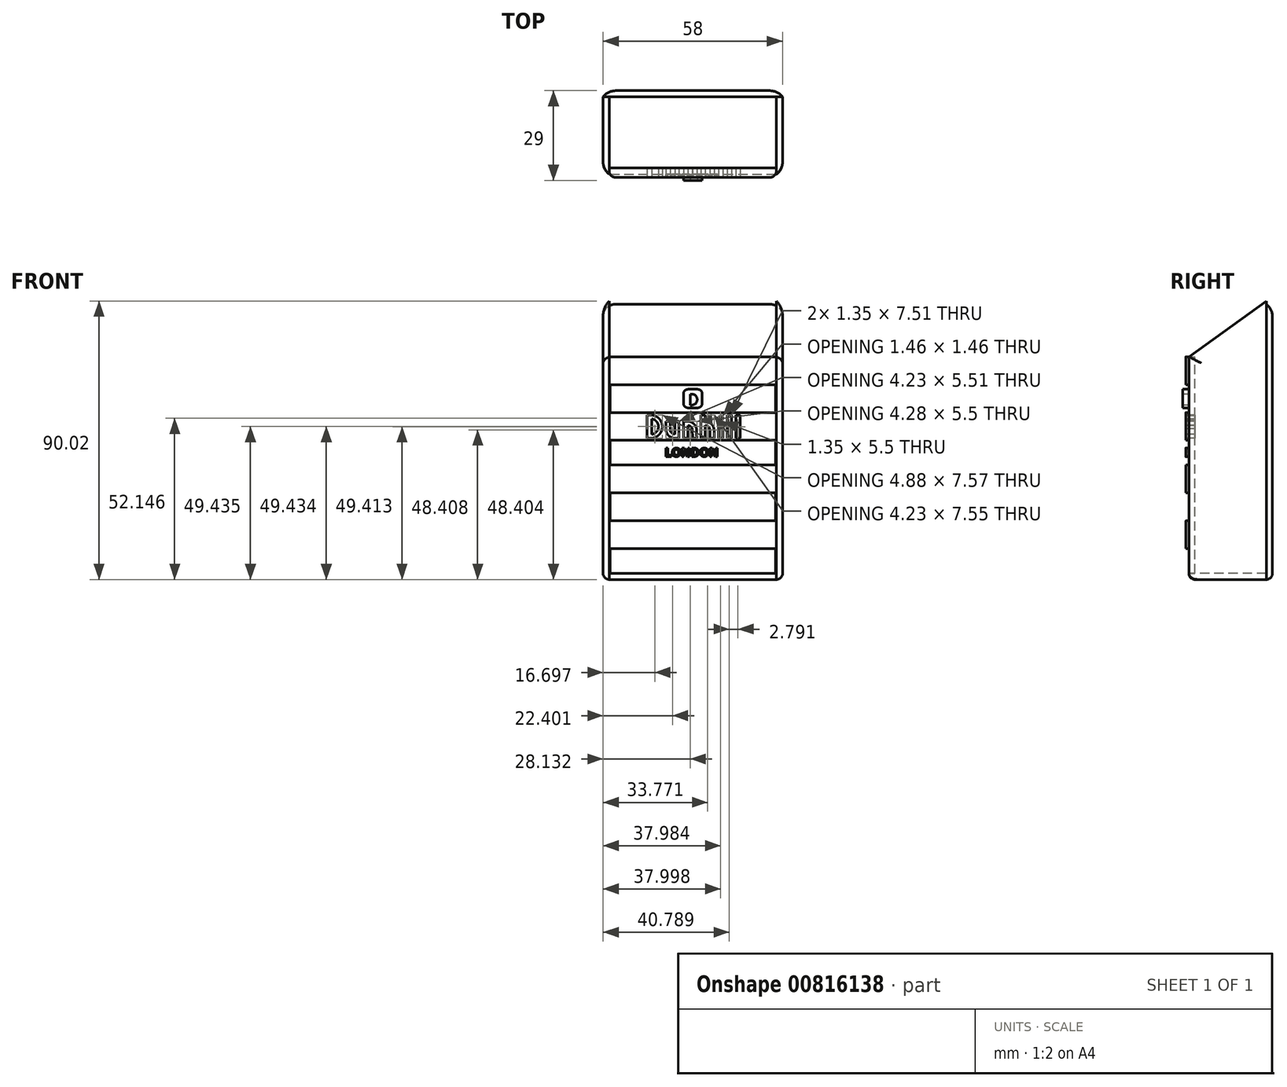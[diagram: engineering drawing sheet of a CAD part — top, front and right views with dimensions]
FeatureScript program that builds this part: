
annotation { "Feature Type Name" : "Feature", "Feature Type Description" : "" }
export const myFeature = defineFeature(function(context is Context, id is Id, definition is map)
    precondition{}
    {
        {
            var Q0;
            Q0=qCreatedBy(makeId("Top.planeOp"),FACE);
            var sketch = newSketch(context, id + "F0", { "sketchPlane" : qUnion([Q0])});
            skLineSegment(sketch, "E0.bottom", {"start": v(-3.76, 0) * mm, "end": v(50.24, 0) * mm});
            skLineSegment(sketch, "E0.top", {"start": v(-3.76, -25) * mm, "end": v(50.24, -25) * mm});
            skLineSegment(sketch, "E0.left", {"start": v(-3.76, 0) * mm, "end": v(-3.76, -25) * mm});
            skLineSegment(sketch, "E0.right", {"start": v(50.24, 0) * mm, "end": v(50.24, -25) * mm});
            skSolve(sketch);
        }
        {
            var Q0;
            Q0=qCreatedBy(makeId("Front.planeOp"),FACE);
            var sketch = newSketch(context, id + "F1", { "sketchPlane" : qUnion([Q0])});
            skLineSegment(sketch, "E1.bottom", {"start": v(-5.76, -2) * mm, "end": v(52.24, -2) * mm});
            skLineSegment(sketch, "E1.top", {"start": v(-5.76, 88) * mm, "end": v(52.24, 88) * mm});
            skLineSegment(sketch, "E1.left", {"start": v(-5.76, -2) * mm, "end": v(-5.76, 88) * mm});
            skLineSegment(sketch, "E1.right", {"start": v(52.24, -2) * mm, "end": v(52.24, 88) * mm});
            skSolve(sketch);
        }
        {
            var Q0;
            Q0=makeQuery(id+"F0.imprint","IMPRINT",FACE,{"disambiguationData":[TD([[makeQuery(id+"F0.imprint","IMPRINT",EDGE,{"derivedFrom":sQuery(id+"F0.wireOp",EDGE,"E0.bottom")}),-1.0]])]});
            extrude(context, id + "F2", {"entities" : qUnion([Q0]), "oppositeDirection" : true, "depth" : 2 * mm, "offsetDistance" : 25 * mm});
        }
        {
            var Q0;
            Q0=makeQuery(id+"F2.opExtrude","SWEPT_FACE",FACE,{"disambiguationData":[OSD([sQuery(id+"F0.wireOp",EDGE,"E0.top")])]});
            cPlane(context, id + "F3", {"entities" : qUnion([Q0]), "cplaneType" : CPlaneType.OFFSET, "offset" : 2 * mm, "oppositeDirection" : true, "width" : 150 * mm, "height" : 150 * mm});
        }
        {
            var Q0;
            Q0=qCreatedBy(id+"F3.planeOp",FACE);
            var sketch = newSketch(context, id + "F4", { "sketchPlane" : qUnion([Q0])});
            skLineSegment(sketch, "E2.bottom", {"start": v(-3.77, 0) * mm, "end": v(50.23, 0) * mm});
            skLineSegment(sketch, "E2.top", {"start": v(-3.77, 70) * mm, "end": v(50.23, 70) * mm});
            skLineSegment(sketch, "E2.left", {"start": v(-3.77, 0) * mm, "end": v(-3.77, 70) * mm});
            skLineSegment(sketch, "E2.right", {"start": v(50.23, 0) * mm, "end": v(50.23, 70) * mm});
            skSolve(sketch);
        }
        {
            var Q0;
            Q0=makeQuery(id+"F2.opExtrude","SWEPT_FACE",FACE,{"disambiguationData":[OSD([sQuery(id+"F0.wireOp",EDGE,"E0.right")])]});
            cPlane(context, id + "F5", {"entities" : qUnion([Q0]), "cplaneType" : CPlaneType.OFFSET, "offset" : 0 * mm, "width" : 150 * mm, "height" : 150 * mm});
        }
        {
            var Q0;
            Q0=qCreatedBy(id+"F5.planeOp",FACE);
            var sketch = newSketch(context, id + "F6", { "sketchPlane" : qUnion([Q0])});
            skLineSegment(sketch, "E3", {"start": v(-25, -2) * mm, "end": v(0, -2) * mm});
            skLineSegment(sketch, "E4", {"start": v(0, -2) * mm, "end": v(0, 88.02) * mm});
            skLineSegment(sketch, "E5", {"start": v(0, 88.02) * mm, "end": v(-25, 70) * mm});
            skLineSegment(sketch, "E6", {"start": v(-25, 70) * mm, "end": v(-25, -2) * mm});
            skSolve(sketch);
        }
        {
            var Q0;
            Q0=makeQuery(id+"F2.opExtrude","SWEPT_FACE",FACE,{"disambiguationData":[OSD([sQuery(id+"F0.wireOp",EDGE,"E0.left")])]});
            cPlane(context, id + "F7", {"entities" : qUnion([Q0]), "cplaneType" : CPlaneType.OFFSET, "offset" : 0 * mm, "width" : 150 * mm, "height" : 150 * mm});
        }
        {
            var Q0;
            Q0=qCreatedBy(id+"F7.planeOp",FACE);
            var sketch = newSketch(context, id + "F8", { "sketchPlane" : qUnion([Q0])});
            skLineSegment(sketch, "E7", {"start": v(0, -2) * mm, "end": v(24.96, -2) * mm});
            skLineSegment(sketch, "E8", {"start": v(24.96, -2) * mm, "end": v(24.96, 70) * mm});
            skLineSegment(sketch, "E9", {"start": v(24.96, 70) * mm, "end": v(0, 88) * mm});
            skLineSegment(sketch, "E10", {"start": v(0, 88) * mm, "end": v(0, -2) * mm});
            skSolve(sketch);
        }
        {
            var Q0;
            Q0=makeQuery(id+"F6.imprint","IMPRINT",FACE,{"disambiguationData":[TD([[makeQuery(id+"F6.imprint","IMPRINT",EDGE,{"derivedFrom":sQuery(id+"F6.wireOp",EDGE,"E3")}),1.0]])]});
            extrude(context, id + "F9", {"entities" : qUnion([Q0]), "depth" : 2 * mm, "offsetDistance" : 25 * mm});
        }
        {
            var Q0;
            Q0=makeQuery(id+"F4.imprint","IMPRINT",FACE,{"disambiguationData":[TD([[makeQuery(id+"F4.imprint","IMPRINT",EDGE,{"derivedFrom":sQuery(id+"F4.wireOp",EDGE,"E2.bottom")}),1.0]])]});
            extrude(context, id + "F10", {"entities" : qUnion([Q0]), "depth" : 2 * mm, "offsetDistance" : 25 * mm});
        }
        {
            var Q0;
            Q0=makeQuery(id+"F8.imprint","IMPRINT",FACE,{"disambiguationData":[TD([[makeQuery(id+"F8.imprint","IMPRINT",EDGE,{"derivedFrom":sQuery(id+"F8.wireOp",EDGE,"E7")}),1.0]])]});
            extrude(context, id + "F11", {"entities" : qUnion([Q0]), "depth" : 2 * mm, "offsetDistance" : 25 * mm});
        }
        {
            var Q0;
            Q0=makeQuery(id+"F1.imprint","IMPRINT",FACE,{"disambiguationData":[TD([[makeQuery(id+"F1.imprint","IMPRINT",EDGE,{"derivedFrom":sQuery(id+"F1.wireOp",EDGE,"E1.bottom")}),1.0]])]});
            extrude(context, id + "F12", {"entities" : qUnion([Q0]), "oppositeDirection" : true, "depth" : 2 * mm, "offsetDistance" : 25 * mm});
        }
        {
            var Q0;
            Q0=makeQuery(id+"F9.opExtrude","CAP_EDGE",EDGE,{"disambiguationData":[OSD([sQuery(id+"F6.wireOp",EDGE,"E6")])],"isStart":false});
            var Q1;
            Q1=makeQuery(id+"F11.opExtrude","CAP_EDGE",EDGE,{"disambiguationData":[OSD([sQuery(id+"F8.wireOp",EDGE,"E8")])],"isStart":false});
            var Q2;
            Q2=makeQuery(id+"F12.opExtrude","CAP_EDGE",EDGE,{"disambiguationData":[OSD([sQuery(id+"F1.wireOp",EDGE,"E1.left")])],"isStart":false});
            var Q3;
            Q3=makeQuery(id+"F12.opExtrude","CAP_EDGE",EDGE,{"disambiguationData":[OSD([sQuery(id+"F1.wireOp",EDGE,"E1.right")])],"isStart":false});
            fillet(context, id + "F13", {"entities" : qUnion([Q0, Q1, Q2, Q3]), "radius" : 5 * mm, "tangentPropagation" : true, "allowEdgeOverflow" : false});
        }
        {
            var Q0;
            Q0=makeQuery(id+"F12.opExtrude","CAP_EDGE",EDGE,{"disambiguationData":[OSD([sQuery(id+"F1.wireOp",EDGE,"E1.bottom")])],"isStart":false});
            var Q1;
            Q1=makeQuery(id+"F11.opExtrude","CAP_EDGE",EDGE,{"disambiguationData":[OSD([sQuery(id+"F8.wireOp",EDGE,"E7")])],"isStart":false});
            var Q2;
            Q2=makeQuery(id+"F9.opExtrude","CAP_EDGE",EDGE,{"disambiguationData":[OSD([sQuery(id+"F6.wireOp",EDGE,"E3")])],"isStart":false});
            fillet(context, id + "F14", {"entities" : qUnion([Q0, Q1, Q2]), "radius" : 2 * mm, "tangentPropagation" : true, "allowEdgeOverflow" : false});
        }
        {
            var Q0;
            Q0=makeQuery(id+"F2.opExtrude","CAP_EDGE",EDGE,{"disambiguationData":[OSD([sQuery(id+"F0.wireOp",EDGE,"E0.top")])],"isStart":false});
            fillet(context, id + "F15", {"entities" : qUnion([Q0]), "radius" : 2 * mm, "tangentPropagation" : true, "allowEdgeOverflow" : false});
        }
        {
            var Q0;
            {var subQ0=sQuery(id+"F4.wireOp",EDGE,"E2.bottom");var subQ1=sQuery(id+"F4.wireOp",EDGE,"E2.top");var subQ2=sQuery(id+"F4.wireOp",EDGE,"E2.left");var subQ3=sQuery(id+"F4.wireOp",EDGE,"E2.right");Q0=makeQuery(id+"F8PJ3iT0SF2CxUe_6.boolean.opBoolean","SPLIT",FACE,{"disambiguationData":[TD([makeQuery(id+"F10.opExtrude","SWEPT_FACE",FACE,{"disambiguationData":[OSD([subQ0])]})])],"derivedFrom":makeQuery(id+"F10.opExtrude","CAP_FACE",FACE,{"disambiguationData":[OSD([subQ0,subQ1,subQ2,subQ3])],"isStart":false})});}
            var sketch = newSketch(context, id + "F16", { "sketchPlane" : qUnion([Q0])});
            skLineSegment(sketch, "E11.bottom", {"start": v(-3.77, 70) * mm, "end": v(50.23, 70) * mm});
            skLineSegment(sketch, "E11.top", {"start": v(-3.77, 61) * mm, "end": v(50.23, 61) * mm});
            skLineSegment(sketch, "E11.left", {"start": v(-3.77, 70) * mm, "end": v(-3.77, 61) * mm});
            skLineSegment(sketch, "E11.right", {"start": v(50.23, 70) * mm, "end": v(50.23, 61) * mm});
            skLineSegment(sketch, "E12.top", {"start": v(-3.77, 52) * mm, "end": v(50.23, 52) * mm});
            skLineSegment(sketch, "E13.top", {"start": v(-3.77, 43) * mm, "end": v(50.23, 43) * mm});
            skLineSegment(sketch, "E13.left", {"start": v(-3.77, 52) * mm, "end": v(-3.77, 43) * mm});
            skLineSegment(sketch, "E13.right", {"start": v(50.23, 52) * mm, "end": v(50.23, 43) * mm});
            skLineSegment(sketch, "E14.bottom", {"start": v(50.23, 35) * mm, "end": v(-3.77, 35) * mm});
            skLineSegment(sketch, "E14.left", {"start": v(50.23, 35) * mm, "end": v(50.23, 26) * mm});
            skLineSegment(sketch, "E14.right", {"start": v(-3.77, 35) * mm, "end": v(-3.77, 26) * mm});
            skLineSegment(sketch, "E15.bottom", {"start": v(-3.77, 26) * mm, "end": v(50.23, 26) * mm});
            skLineSegment(sketch, "E15.top", {"start": v(-3.77, 17) * mm, "end": v(50.23, 17) * mm});
            skLineSegment(sketch, "E16.top", {"start": v(-3.77, 8) * mm, "end": v(50.23, 8) * mm});
            skLineSegment(sketch, "E16.left", {"start": v(-3.77, 17) * mm, "end": v(-3.77, 8) * mm});
            skLineSegment(sketch, "E16.right", {"start": v(50.23, 17) * mm, "end": v(50.23, 8) * mm});
            skSolve(sketch);
        }
        {
            var Q0;
            Q0=makeQuery(id+"F16.imprint","IMPRINT",FACE,{"disambiguationData":[TD([[makeQuery(id+"F16.imprint","IMPRINT",EDGE,{"derivedFrom":sQuery(id+"F16.wireOp",EDGE,"E11.bottom")}),-1.0]])]});
            var Q1;
            Q1=makeQuery(id+"F16.imprint","IMPRINT",FACE,{"disambiguationData":[TD([[makeQuery(id+"F16.imprint","IMPRINT",EDGE,{"derivedFrom":sQuery(id+"F16.wireOp",EDGE,"E12.top")}),-1.0]])]});
            var Q2;
            Q2=makeQuery(id+"F16.imprint","IMPRINT",FACE,{"disambiguationData":[TD([[makeQuery(id+"F16.imprint","IMPRINT",EDGE,{"derivedFrom":sQuery(id+"F16.wireOp",EDGE,"E14.bottom")}),1.0]])]});
            var Q3;
            Q3=makeQuery(id+"F16.imprint","IMPRINT",FACE,{"disambiguationData":[TD([[makeQuery(id+"F16.imprint","IMPRINT",EDGE,{"derivedFrom":sQuery(id+"F16.wireOp",EDGE,"E15.top")}),-1.0]])]});
            extrude(context, id + "F17", {"entities" : qUnion([Q0, Q1, Q2, Q3]), "operationType" : NewBodyOperationType.ADD, "depth" : 1 * mm, "offsetDistance" : 25 * mm});
        }
        {
            var Q0;
            Q0=makeQuery(id+"F17.opExtrude","CAP_EDGE",EDGE,{"disambiguationData":[OSD([sQuery(id+"F16.wireOp",EDGE,"E11.left")])],"isStart":false});
            var Q1;
            Q1=makeQuery(id+"F17.opExtrude","CAP_EDGE",EDGE,{"disambiguationData":[OSD([sQuery(id+"F16.wireOp",EDGE,"E13.left")])],"isStart":false});
            var Q2;
            Q2=makeQuery(id+"F17.opExtrude","CAP_EDGE",EDGE,{"disambiguationData":[OSD([sQuery(id+"F16.wireOp",EDGE,"E14.right")])],"isStart":false});
            var Q3;
            Q3=makeQuery(id+"F17.opExtrude","CAP_EDGE",EDGE,{"disambiguationData":[OSD([sQuery(id+"F16.wireOp",EDGE,"E16.left")])],"isStart":false});
            var Q4;
            Q4=makeQuery(id+"F17.opExtrude","CAP_EDGE",EDGE,{"disambiguationData":[OSD([sQuery(id+"F16.wireOp",EDGE,"E16.right")])],"isStart":false});
            var Q5;
            Q5=makeQuery(id+"F17.opExtrude","CAP_EDGE",EDGE,{"disambiguationData":[OSD([sQuery(id+"F16.wireOp",EDGE,"E14.left")])],"isStart":false});
            var Q6;
            Q6=makeQuery(id+"F17.opExtrude","CAP_EDGE",EDGE,{"disambiguationData":[OSD([sQuery(id+"F16.wireOp",EDGE,"E13.right")])],"isStart":false});
            var Q7;
            Q7=makeQuery(id+"F17.opExtrude","CAP_EDGE",EDGE,{"disambiguationData":[OSD([sQuery(id+"F16.wireOp",EDGE,"E11.right")])],"isStart":false});
            fillet(context, id + "F18", {"entities" : qUnion([Q0, Q1, Q2, Q3, Q4, Q5, Q6, Q7]), "radius" : 2 * mm, "tangentPropagation" : true, "allowEdgeOverflow" : false});
        }
        {
            var Q0;
            Q0=makeQuery(id+"F17.opExtrude","CAP_FACE",FACE,{"disambiguationData":[OSD([sQuery(id+"F16.wireOp",EDGE,"E12.top"),sQuery(id+"F16.wireOp",EDGE,"E13.top"),sQuery(id+"F16.wireOp",EDGE,"E13.left"),sQuery(id+"F16.wireOp",EDGE,"E13.right")])],"isStart":false});
            var sketch = newSketch(context, id + "F19", { "sketchPlane" : qUnion([Q0])});
            skLineSegment(sketch, "E17", {"start": v(8.5, 47.43) * mm, "end": v(8.5, 43.65) * mm});
            skLineSegment(sketch, "E18", {"start": v(8.5, 43.65) * mm, "end": v(9.37, 43.67) * mm});
            skArc(sketch, "E19", {"start": v(9.37, 43.67) * mm, "mid": v(9.7, 43.68) * mm, "end": v(10.05, 43.7) * mm});
            skArc(sketch, "E20", {"start": v(10.05, 43.7) * mm, "mid": v(10.27, 43.72) * mm, "end": v(10.49, 43.76) * mm});
            skArc(sketch, "E21", {"start": v(10.49, 43.76) * mm, "mid": v(10.68, 43.8) * mm, "end": v(10.86, 43.87) * mm});
            skArc(sketch, "E22", {"start": v(10.86, 43.87) * mm, "mid": v(11.09, 43.96) * mm, "end": v(11.3, 44.07) * mm});
            skArc(sketch, "E23", {"start": v(11.3, 44.07) * mm, "mid": v(11.65, 44.26) * mm, "end": v(11.96, 44.48) * mm});
            skArc(sketch, "E24", {"start": v(11.96, 44.48) * mm, "mid": v(12.25, 44.74) * mm, "end": v(12.51, 45.02) * mm});
            skArc(sketch, "E25", {"start": v(12.51, 45.02) * mm, "mid": v(12.74, 45.33) * mm, "end": v(12.94, 45.66) * mm});
            skArc(sketch, "E26", {"start": v(12.94, 45.66) * mm, "mid": v(13.1, 46.02) * mm, "end": v(13.24, 46.39) * mm});
            skArc(sketch, "E27", {"start": v(13.24, 46.39) * mm, "mid": v(13.3, 46.6) * mm, "end": v(13.33, 46.8) * mm});
            skArc(sketch, "E28", {"start": v(13.33, 46.8) * mm, "mid": v(13.36, 47.04) * mm, "end": v(13.37, 47.27) * mm});
            skArc(sketch, "E29", {"start": v(13.37, 47.27) * mm, "mid": v(13.38, 47.5) * mm, "end": v(13.37, 47.74) * mm});
            skArc(sketch, "E30", {"start": v(13.37, 47.74) * mm, "mid": v(13.34, 47.96) * mm, "end": v(13.3, 48.17) * mm});
            skArc(sketch, "E31", {"start": v(13.3, 48.17) * mm, "mid": v(13.2, 48.6) * mm, "end": v(13.03, 49.01) * mm});
            skArc(sketch, "E32", {"start": v(13.03, 49.01) * mm, "mid": v(12.82, 49.4) * mm, "end": v(12.57, 49.76) * mm});
            skArc(sketch, "E33", {"start": v(12.57, 49.76) * mm, "mid": v(12.28, 50.08) * mm, "end": v(11.95, 50.37) * mm});
            skArc(sketch, "E34", {"start": v(11.95, 50.37) * mm, "mid": v(11.59, 50.63) * mm, "end": v(11.2, 50.84) * mm});
            skArc(sketch, "E35", {"start": v(11.2, 50.84) * mm, "mid": v(11, 50.93) * mm, "end": v(10.79, 51) * mm});
            skArc(sketch, "E36", {"start": v(10.79, 51) * mm, "mid": v(10.6, 51.06) * mm, "end": v(10.4, 51.1) * mm});
            skArc(sketch, "E37", {"start": v(10.4, 51.1) * mm, "mid": v(10.19, 51.14) * mm, "end": v(9.96, 51.17) * mm});
            skArc(sketch, "E38", {"start": v(9.96, 51.17) * mm, "mid": v(9.65, 51.18) * mm, "end": v(9.33, 51.2) * mm});
            skLineSegment(sketch, "E39", {"start": v(9.33, 51.2) * mm, "end": v(8.5, 51.22) * mm});
            skLineSegment(sketch, "E40", {"start": v(8.5, 51.22) * mm, "end": v(8.5, 47.43) * mm});
            skArc(sketch, "E41", {"start": v(10.45, 49.8) * mm, "mid": v(10.71, 49.7) * mm, "end": v(10.96, 49.56) * mm});
            skArc(sketch, "E42", {"start": v(10.96, 49.56) * mm, "mid": v(11.2, 49.38) * mm, "end": v(11.42, 49.18) * mm});
            skArc(sketch, "E43", {"start": v(11.42, 49.18) * mm, "mid": v(11.62, 48.95) * mm, "end": v(11.8, 48.7) * mm});
            skArc(sketch, "E44", {"start": v(11.8, 48.7) * mm, "mid": v(11.93, 48.43) * mm, "end": v(12.04, 48.15) * mm});
            skArc(sketch, "E45", {"start": v(12.04, 48.15) * mm, "mid": v(12.08, 47.98) * mm, "end": v(12.11, 47.8) * mm});
            skArc(sketch, "E46", {"start": v(12.11, 47.8) * mm, "mid": v(12.13, 47.6) * mm, "end": v(12.13, 47.4) * mm});
            skArc(sketch, "E47", {"start": v(12.13, 47.4) * mm, "mid": v(12.12, 47.2) * mm, "end": v(12.1, 47) * mm});
            skArc(sketch, "E48", {"start": v(12.1, 47) * mm, "mid": v(12.06, 46.81) * mm, "end": v(12.01, 46.63) * mm});
            skArc(sketch, "E49", {"start": v(12.01, 46.63) * mm, "mid": v(11.9, 46.35) * mm, "end": v(11.74, 46.08) * mm});
            skArc(sketch, "E50", {"start": v(11.74, 46.08) * mm, "mid": v(11.56, 45.83) * mm, "end": v(11.35, 45.6) * mm});
            skArc(sketch, "E51", {"start": v(11.35, 45.6) * mm, "mid": v(11.12, 45.4) * mm, "end": v(10.87, 45.24) * mm});
            skArc(sketch, "E52", {"start": v(10.87, 45.24) * mm, "mid": v(10.6, 45.1) * mm, "end": v(10.3, 45) * mm});
            skArc(sketch, "E53", {"start": v(10.3, 45) * mm, "mid": v(10.19, 44.98) * mm, "end": v(10.07, 44.99) * mm});
            skArc(sketch, "E54", {"start": v(10.07, 44.99) * mm, "mid": v(10, 45.03) * mm, "end": v(9.96, 45.1) * mm});
            skArc(sketch, "E55", {"start": v(9.96, 45.1) * mm, "mid": v(9.94, 45.28) * mm, "end": v(9.94, 45.46) * mm});
            skArc(sketch, "E56", {"start": v(9.94, 45.46) * mm, "mid": v(9.93, 46.45) * mm, "end": v(9.93, 47.43) * mm});
            skLineSegment(sketch, "E57", {"start": v(9.93, 47.43) * mm, "end": v(9.93, 49.93) * mm});
            skLineSegment(sketch, "E58", {"start": v(9.93, 49.93) * mm, "end": v(10.07, 49.91) * mm});
            skArc(sketch, "E59", {"start": v(10.07, 49.91) * mm, "mid": v(10.1, 49.9) * mm, "end": v(10.13, 49.9) * mm});
            skArc(sketch, "E60", {"start": v(10.13, 49.9) * mm, "mid": v(10.18, 49.88) * mm, "end": v(10.23, 49.87) * mm});
            skArc(sketch, "E61", {"start": v(10.23, 49.87) * mm, "mid": v(10.29, 49.85) * mm, "end": v(10.34, 49.84) * mm});
            skArc(sketch, "E62", {"start": v(10.34, 49.84) * mm, "mid": v(10.4, 49.82) * mm, "end": v(10.45, 49.8) * mm});
            skLineSegment(sketch, "E63", {"start": v(25.9, 47.43) * mm, "end": v(25.9, 43.66) * mm});
            skLineSegment(sketch, "E64", {"start": v(25.9, 43.66) * mm, "end": v(26.57, 43.66) * mm});
            skLineSegment(sketch, "E65", {"start": v(26.57, 43.66) * mm, "end": v(27.25, 43.66) * mm});
            skLineSegment(sketch, "E66", {"start": v(27.25, 43.66) * mm, "end": v(27.25, 45.74) * mm});
            skLineSegment(sketch, "E67", {"start": v(27.25, 45.74) * mm, "end": v(27.25, 47.81) * mm});
            skLineSegment(sketch, "E68", {"start": v(27.25, 47.81) * mm, "end": v(27.46, 47.79) * mm});
            skArc(sketch, "E69", {"start": v(27.46, 47.79) * mm, "mid": v(27.62, 47.76) * mm, "end": v(27.78, 47.71) * mm});
            skArc(sketch, "E70", {"start": v(27.78, 47.71) * mm, "mid": v(27.94, 47.64) * mm, "end": v(28.09, 47.55) * mm});
            skArc(sketch, "E71", {"start": v(28.09, 47.55) * mm, "mid": v(28.22, 47.45) * mm, "end": v(28.35, 47.33) * mm});
            skArc(sketch, "E72", {"start": v(28.35, 47.33) * mm, "mid": v(28.45, 47.21) * mm, "end": v(28.54, 47.07) * mm});
            skArc(sketch, "E73", {"start": v(28.54, 47.07) * mm, "mid": v(28.6, 46.93) * mm, "end": v(28.67, 46.77) * mm});
            skArc(sketch, "E74", {"start": v(28.67, 46.77) * mm, "mid": v(28.7, 46.62) * mm, "end": v(28.73, 46.46) * mm});
            skArc(sketch, "E75", {"start": v(28.73, 46.46) * mm, "mid": v(28.75, 46.22) * mm, "end": v(28.76, 46) * mm});
            skArc(sketch, "E76", {"start": v(28.76, 46) * mm, "mid": v(28.77, 45.5) * mm, "end": v(28.77, 45.02) * mm});
            skLineSegment(sketch, "E77", {"start": v(28.77, 45.02) * mm, "end": v(28.77, 43.66) * mm});
            skLineSegment(sketch, "E78", {"start": v(28.77, 43.66) * mm, "end": v(29.45, 43.66) * mm});
            skLineSegment(sketch, "E79", {"start": v(29.45, 43.66) * mm, "end": v(30.12, 43.66) * mm});
            skLineSegment(sketch, "E80", {"start": v(30.12, 43.66) * mm, "end": v(30.12, 45.02) * mm});
            skArc(sketch, "E81", {"start": v(30.12, 45.02) * mm, "mid": v(30.12, 45.3) * mm, "end": v(30.12, 45.57) * mm});
            skArc(sketch, "E82", {"start": v(30.12, 45.57) * mm, "mid": v(30.12, 45.82) * mm, "end": v(30.11, 46.07) * mm});
            skArc(sketch, "E83", {"start": v(30.11, 46.07) * mm, "mid": v(30.1, 46.27) * mm, "end": v(30.1, 46.48) * mm});
            skArc(sketch, "E84", {"start": v(30.1, 46.48) * mm, "mid": v(30.1, 46.57) * mm, "end": v(30.08, 46.65) * mm});
            skArc(sketch, "E85", {"start": v(30.08, 46.65) * mm, "mid": v(30, 47.02) * mm, "end": v(29.87, 47.37) * mm});
            skArc(sketch, "E86", {"start": v(29.87, 47.37) * mm, "mid": v(29.7, 47.7) * mm, "end": v(29.5, 48) * mm});
            skArc(sketch, "E87", {"start": v(29.5, 48) * mm, "mid": v(29.26, 48.28) * mm, "end": v(28.98, 48.53) * mm});
            skArc(sketch, "E88", {"start": v(28.98, 48.53) * mm, "mid": v(28.67, 48.74) * mm, "end": v(28.33, 48.92) * mm});
            skArc(sketch, "E89", {"start": v(28.33, 48.92) * mm, "mid": v(28.22, 48.97) * mm, "end": v(28.1, 49) * mm});
            skArc(sketch, "E90", {"start": v(28.1, 49) * mm, "mid": v(27.97, 49.05) * mm, "end": v(27.84, 49.09) * mm});
            skArc(sketch, "E91", {"start": v(27.84, 49.09) * mm, "mid": v(27.72, 49.12) * mm, "end": v(27.6, 49.14) * mm});
            skArc(sketch, "E92", {"start": v(27.6, 49.14) * mm, "mid": v(27.5, 49.15) * mm, "end": v(27.4, 49.16) * mm});
            skLineSegment(sketch, "E93", {"start": v(27.4, 49.16) * mm, "end": v(27.25, 49.16) * mm});
            skLineSegment(sketch, "E94", {"start": v(27.25, 49.16) * mm, "end": v(27.25, 50.18) * mm});
            skLineSegment(sketch, "E95", {"start": v(27.25, 50.18) * mm, "end": v(27.25, 51.2) * mm});
            skLineSegment(sketch, "E96", {"start": v(27.25, 51.2) * mm, "end": v(26.57, 51.2) * mm});
            skLineSegment(sketch, "E97", {"start": v(26.57, 51.2) * mm, "end": v(25.9, 51.2) * mm});
            skLineSegment(sketch, "E98", {"start": v(25.9, 51.2) * mm, "end": v(25.9, 47.43) * mm});
            skLineSegment(sketch, "E99", {"start": v(34.35, 47.41) * mm, "end": v(34.35, 43.66) * mm});
            skLineSegment(sketch, "E100", {"start": v(34.35, 43.66) * mm, "end": v(35.03, 43.66) * mm});
            skLineSegment(sketch, "E101", {"start": v(35.03, 43.66) * mm, "end": v(35.7, 43.66) * mm});
            skLineSegment(sketch, "E102", {"start": v(35.7, 43.66) * mm, "end": v(35.7, 47.41) * mm});
            skLineSegment(sketch, "E103", {"start": v(35.7, 47.41) * mm, "end": v(35.7, 51.17) * mm});
            skLineSegment(sketch, "E104", {"start": v(35.7, 51.17) * mm, "end": v(35.03, 51.17) * mm});
            skLineSegment(sketch, "E105", {"start": v(35.03, 51.17) * mm, "end": v(34.35, 51.17) * mm});
            skLineSegment(sketch, "E106", {"start": v(34.35, 51.17) * mm, "end": v(34.35, 47.41) * mm});
            skLineSegment(sketch, "E107", {"start": v(37.14, 47.41) * mm, "end": v(37.14, 43.66) * mm});
            skLineSegment(sketch, "E108", {"start": v(37.14, 43.66) * mm, "end": v(37.82, 43.66) * mm});
            skLineSegment(sketch, "E109", {"start": v(37.82, 43.66) * mm, "end": v(38.5, 43.66) * mm});
            skLineSegment(sketch, "E110", {"start": v(38.5, 43.66) * mm, "end": v(38.5, 47.41) * mm});
            skLineSegment(sketch, "E111", {"start": v(38.5, 47.41) * mm, "end": v(38.5, 51.17) * mm});
            skLineSegment(sketch, "E112", {"start": v(38.5, 51.17) * mm, "end": v(37.82, 51.17) * mm});
            skLineSegment(sketch, "E113", {"start": v(37.82, 51.17) * mm, "end": v(37.14, 51.17) * mm});
            skLineSegment(sketch, "E114", {"start": v(37.14, 51.17) * mm, "end": v(37.14, 47.41) * mm});
            skArc(sketch, "E115", {"start": v(31.9, 50.8) * mm, "mid": v(31.75, 50.7) * mm, "end": v(31.63, 50.57) * mm});
            skArc(sketch, "E116", {"start": v(31.63, 50.57) * mm, "mid": v(31.55, 50.43) * mm, "end": v(31.5, 50.26) * mm});
            skArc(sketch, "E117", {"start": v(31.5, 50.26) * mm, "mid": v(31.5, 50.1) * mm, "end": v(31.53, 49.92) * mm});
            skArc(sketch, "E118", {"start": v(31.53, 49.92) * mm, "mid": v(31.6, 49.77) * mm, "end": v(31.72, 49.63) * mm});
            skArc(sketch, "E119", {"start": v(31.72, 49.63) * mm, "mid": v(31.85, 49.52) * mm, "end": v(32, 49.45) * mm});
            skArc(sketch, "E120", {"start": v(32, 49.45) * mm, "mid": v(32.17, 49.42) * mm, "end": v(32.34, 49.42) * mm});
            skArc(sketch, "E121", {"start": v(32.34, 49.42) * mm, "mid": v(32.5, 49.47) * mm, "end": v(32.65, 49.55) * mm});
            skArc(sketch, "E122", {"start": v(32.65, 49.55) * mm, "mid": v(32.77, 49.67) * mm, "end": v(32.86, 49.81) * mm});
            skArc(sketch, "E123", {"start": v(32.86, 49.81) * mm, "mid": v(32.9, 49.9) * mm, "end": v(32.93, 49.98) * mm});
            skArc(sketch, "E124", {"start": v(32.93, 49.98) * mm, "mid": v(32.95, 50.06) * mm, "end": v(32.95, 50.15) * mm});
            skArc(sketch, "E125", {"start": v(32.95, 50.15) * mm, "mid": v(32.95, 50.23) * mm, "end": v(32.94, 50.3) * mm});
            skArc(sketch, "E126", {"start": v(32.94, 50.3) * mm, "mid": v(32.91, 50.39) * mm, "end": v(32.88, 50.46) * mm});
            skArc(sketch, "E127", {"start": v(32.88, 50.46) * mm, "mid": v(32.8, 50.59) * mm, "end": v(32.7, 50.7) * mm});
            skArc(sketch, "E128", {"start": v(32.7, 50.7) * mm, "mid": v(32.59, 50.78) * mm, "end": v(32.46, 50.84) * mm});
            skArc(sketch, "E129", {"start": v(32.46, 50.84) * mm, "mid": v(32.32, 50.87) * mm, "end": v(32.18, 50.87) * mm});
            skArc(sketch, "E130", {"start": v(32.18, 50.87) * mm, "mid": v(32.03, 50.85) * mm, "end": v(31.9, 50.8) * mm});
            skArc(sketch, "E131", {"start": v(14.54, 47.65) * mm, "mid": v(14.55, 47.1) * mm, "end": v(14.56, 46.56) * mm});
            skArc(sketch, "E132", {"start": v(14.56, 46.56) * mm, "mid": v(14.57, 46.33) * mm, "end": v(14.6, 46.1) * mm});
            skArc(sketch, "E133", {"start": v(14.6, 46.1) * mm, "mid": v(14.62, 45.92) * mm, "end": v(14.67, 45.76) * mm});
            skArc(sketch, "E134", {"start": v(14.67, 45.76) * mm, "mid": v(14.75, 45.56) * mm, "end": v(14.83, 45.36) * mm});
            skArc(sketch, "E135", {"start": v(14.83, 45.36) * mm, "mid": v(14.98, 45.1) * mm, "end": v(15.15, 44.84) * mm});
            skArc(sketch, "E136", {"start": v(15.15, 44.84) * mm, "mid": v(15.34, 44.61) * mm, "end": v(15.55, 44.4) * mm});
            skArc(sketch, "E137", {"start": v(15.55, 44.4) * mm, "mid": v(15.8, 44.22) * mm, "end": v(16.05, 44.06) * mm});
            skArc(sketch, "E138", {"start": v(16.05, 44.06) * mm, "mid": v(16.34, 43.92) * mm, "end": v(16.64, 43.8) * mm});
            skArc(sketch, "E139", {"start": v(16.64, 43.8) * mm, "mid": v(16.75, 43.76) * mm, "end": v(16.86, 43.73) * mm});
            skArc(sketch, "E140", {"start": v(16.86, 43.73) * mm, "mid": v(16.96, 43.71) * mm, "end": v(17.05, 43.7) * mm});
            skArc(sketch, "E141", {"start": v(17.05, 43.7) * mm, "mid": v(17.18, 43.69) * mm, "end": v(17.31, 43.68) * mm});
            skArc(sketch, "E142", {"start": v(17.31, 43.68) * mm, "mid": v(17.59, 43.67) * mm, "end": v(17.86, 43.67) * mm});
            skLineSegment(sketch, "E143", {"start": v(17.86, 43.67) * mm, "end": v(18.76, 43.65) * mm});
            skLineSegment(sketch, "E144", {"start": v(18.76, 43.65) * mm, "end": v(18.76, 46.4) * mm});
            skLineSegment(sketch, "E145", {"start": v(18.76, 46.4) * mm, "end": v(18.76, 49.16) * mm});
            skLineSegment(sketch, "E146", {"start": v(18.76, 49.16) * mm, "end": v(18.08, 49.16) * mm});
            skLineSegment(sketch, "E147", {"start": v(18.08, 49.16) * mm, "end": v(17.4, 49.16) * mm});
            skLineSegment(sketch, "E148", {"start": v(17.4, 49.16) * mm, "end": v(17.4, 47.08) * mm});
            skLineSegment(sketch, "E149", {"start": v(17.4, 47.08) * mm, "end": v(17.4, 45) * mm});
            skLineSegment(sketch, "E150", {"start": v(17.4, 45) * mm, "end": v(17.23, 45.03) * mm});
            skArc(sketch, "E151", {"start": v(17.23, 45.03) * mm, "mid": v(17.19, 45.04) * mm, "end": v(17.15, 45.05) * mm});
            skArc(sketch, "E152", {"start": v(17.15, 45.05) * mm, "mid": v(17.1, 45.06) * mm, "end": v(17.04, 45.08) * mm});
            skArc(sketch, "E153", {"start": v(17.04, 45.08) * mm, "mid": v(16.98, 45.1) * mm, "end": v(16.93, 45.11) * mm});
            skArc(sketch, "E154", {"start": v(16.93, 45.11) * mm, "mid": v(16.88, 45.13) * mm, "end": v(16.83, 45.15) * mm});
            skArc(sketch, "E155", {"start": v(16.83, 45.15) * mm, "mid": v(16.7, 45.2) * mm, "end": v(16.6, 45.27) * mm});
            skArc(sketch, "E156", {"start": v(16.6, 45.27) * mm, "mid": v(16.47, 45.37) * mm, "end": v(16.35, 45.48) * mm});
            skArc(sketch, "E157", {"start": v(16.35, 45.48) * mm, "mid": v(16.24, 45.6) * mm, "end": v(16.14, 45.73) * mm});
            skArc(sketch, "E158", {"start": v(16.14, 45.73) * mm, "mid": v(16.06, 45.85) * mm, "end": v(16, 45.98) * mm});
            skArc(sketch, "E159", {"start": v(16, 45.98) * mm, "mid": v(15.97, 46.07) * mm, "end": v(15.95, 46.17) * mm});
            skArc(sketch, "E160", {"start": v(15.95, 46.17) * mm, "mid": v(15.93, 46.28) * mm, "end": v(15.92, 46.39) * mm});
            skArc(sketch, "E161", {"start": v(15.92, 46.39) * mm, "mid": v(15.9, 46.57) * mm, "end": v(15.9, 46.75) * mm});
            skArc(sketch, "E162", {"start": v(15.9, 46.75) * mm, "mid": v(15.9, 47.22) * mm, "end": v(15.9, 47.7) * mm});
            skLineSegment(sketch, "E163", {"start": v(15.9, 47.7) * mm, "end": v(15.88, 49.16) * mm});
            skLineSegment(sketch, "E164", {"start": v(15.88, 49.16) * mm, "end": v(15.2, 49.16) * mm});
            skLineSegment(sketch, "E165", {"start": v(15.2, 49.16) * mm, "end": v(14.52, 49.16) * mm});
            skLineSegment(sketch, "E166", {"start": v(14.52, 49.16) * mm, "end": v(14.54, 47.65) * mm});
            skLineSegment(sketch, "E167", {"start": v(20.23, 46.4) * mm, "end": v(20.23, 43.66) * mm});
            skLineSegment(sketch, "E168", {"start": v(20.23, 43.66) * mm, "end": v(20.91, 43.66) * mm});
            skLineSegment(sketch, "E169", {"start": v(20.91, 43.66) * mm, "end": v(21.59, 43.66) * mm});
            skLineSegment(sketch, "E170", {"start": v(21.59, 43.66) * mm, "end": v(21.59, 45.73) * mm});
            skLineSegment(sketch, "E171", {"start": v(21.59, 45.73) * mm, "end": v(21.59, 47.8) * mm});
            skLineSegment(sketch, "E172", {"start": v(21.59, 47.8) * mm, "end": v(21.7, 47.8) * mm});
            skArc(sketch, "E173", {"start": v(21.7, 47.8) * mm, "mid": v(21.74, 47.8) * mm, "end": v(21.77, 47.8) * mm});
            skArc(sketch, "E174", {"start": v(21.77, 47.8) * mm, "mid": v(21.82, 47.79) * mm, "end": v(21.87, 47.78) * mm});
            skArc(sketch, "E175", {"start": v(21.87, 47.78) * mm, "mid": v(21.93, 47.77) * mm, "end": v(21.98, 47.75) * mm});
            skArc(sketch, "E176", {"start": v(21.98, 47.75) * mm, "mid": v(22.04, 47.74) * mm, "end": v(22.1, 47.72) * mm});
            skArc(sketch, "E177", {"start": v(22.1, 47.72) * mm, "mid": v(22.23, 47.67) * mm, "end": v(22.35, 47.6) * mm});
            skArc(sketch, "E178", {"start": v(22.35, 47.6) * mm, "mid": v(22.47, 47.53) * mm, "end": v(22.59, 47.44) * mm});
            skArc(sketch, "E179", {"start": v(22.59, 47.44) * mm, "mid": v(22.7, 47.33) * mm, "end": v(22.8, 47.21) * mm});
            skArc(sketch, "E180", {"start": v(22.8, 47.21) * mm, "mid": v(22.88, 47.08) * mm, "end": v(22.95, 46.95) * mm});
            skLineSegment(sketch, "E181", {"start": v(22.95, 46.95) * mm, "end": v(23.09, 46.68) * mm});
            skLineSegment(sketch, "E182", {"start": v(23.09, 46.68) * mm, "end": v(23.1, 45.17) * mm});
            skLineSegment(sketch, "E183", {"start": v(23.1, 45.17) * mm, "end": v(23.11, 43.66) * mm});
            skLineSegment(sketch, "E184", {"start": v(23.11, 43.66) * mm, "end": v(23.81, 43.66) * mm});
            skLineSegment(sketch, "E185", {"start": v(23.81, 43.66) * mm, "end": v(24.51, 43.66) * mm});
            skLineSegment(sketch, "E186", {"start": v(24.51, 43.66) * mm, "end": v(24.5, 45.13) * mm});
            skArc(sketch, "E187", {"start": v(24.5, 45.13) * mm, "mid": v(24.49, 45.56) * mm, "end": v(24.48, 46) * mm});
            skArc(sketch, "E188", {"start": v(24.48, 46) * mm, "mid": v(24.47, 46.2) * mm, "end": v(24.46, 46.4) * mm});
            skArc(sketch, "E189", {"start": v(24.46, 46.4) * mm, "mid": v(24.45, 46.54) * mm, "end": v(24.44, 46.68) * mm});
            skArc(sketch, "E190", {"start": v(24.44, 46.68) * mm, "mid": v(24.41, 46.8) * mm, "end": v(24.39, 46.91) * mm});
            skArc(sketch, "E191", {"start": v(24.39, 46.91) * mm, "mid": v(24.26, 47.3) * mm, "end": v(24.08, 47.66) * mm});
            skArc(sketch, "E192", {"start": v(24.08, 47.66) * mm, "mid": v(23.86, 47.99) * mm, "end": v(23.6, 48.29) * mm});
            skArc(sketch, "E193", {"start": v(23.6, 48.29) * mm, "mid": v(23.3, 48.55) * mm, "end": v(22.98, 48.76) * mm});
            skArc(sketch, "E194", {"start": v(22.98, 48.76) * mm, "mid": v(22.62, 48.94) * mm, "end": v(22.24, 49.07) * mm});
            skArc(sketch, "E195", {"start": v(22.24, 49.07) * mm, "mid": v(22.14, 49.1) * mm, "end": v(22.04, 49.12) * mm});
            skArc(sketch, "E196", {"start": v(22.04, 49.12) * mm, "mid": v(21.94, 49.13) * mm, "end": v(21.84, 49.14) * mm});
            skArc(sketch, "E197", {"start": v(21.84, 49.14) * mm, "mid": v(21.7, 49.15) * mm, "end": v(21.56, 49.15) * mm});
            skArc(sketch, "E198", {"start": v(21.56, 49.15) * mm, "mid": v(21.32, 49.16) * mm, "end": v(21.09, 49.16) * mm});
            skLineSegment(sketch, "E199", {"start": v(21.09, 49.16) * mm, "end": v(20.23, 49.16) * mm});
            skLineSegment(sketch, "E200", {"start": v(20.23, 49.16) * mm, "end": v(20.23, 46.4) * mm});
            skLineSegment(sketch, "E201", {"start": v(31.56, 46.4) * mm, "end": v(31.56, 43.66) * mm});
            skLineSegment(sketch, "E202", {"start": v(31.56, 43.66) * mm, "end": v(32.24, 43.66) * mm});
            skLineSegment(sketch, "E203", {"start": v(32.24, 43.66) * mm, "end": v(32.92, 43.66) * mm});
            skLineSegment(sketch, "E204", {"start": v(32.92, 43.66) * mm, "end": v(32.92, 46.4) * mm});
            skLineSegment(sketch, "E205", {"start": v(32.92, 46.4) * mm, "end": v(32.92, 49.16) * mm});
            skLineSegment(sketch, "E206", {"start": v(32.92, 49.16) * mm, "end": v(32.24, 49.16) * mm});
            skLineSegment(sketch, "E207", {"start": v(32.24, 49.16) * mm, "end": v(31.56, 49.16) * mm});
            skLineSegment(sketch, "E208", {"start": v(31.56, 49.16) * mm, "end": v(31.56, 46.4) * mm});
            skSolve(sketch);
        }
        {
            var Q0;
            Q0 = qSketchRegion(id + "F19", true);
            extrude(context, id + "F20", {"entities" : qUnion([Q0]), "operationType" : NewBodyOperationType.REMOVE, "oppositeDirection" : true, "depth" : 3 * mm, "offsetDistance" : 25 * mm});
        }
        {
            var Q0;
            {var subQ0=sQuery(id+"F4.wireOp",EDGE,"E2.right");var subQ1=sQuery(id+"F4.wireOp",EDGE,"E2.left");Q0=makeQuery(id+"F17.boolean.opBoolean","SPLIT",FACE,{"disambiguationData":[TD([makeQuery(id+"F17.opExtrude","SWEPT_FACE",FACE,{"disambiguationData":[OSD([sQuery(id+"F16.wireOp",EDGE,"E13.top")])]})])],"derivedFrom":makeQuery(id+"F10.opExtrude","CAP_FACE",FACE,{"disambiguationData":[OSD([sQuery(id+"F4.wireOp",EDGE,"E2.bottom"),sQuery(id+"F4.wireOp",EDGE,"E2.top"),subQ1,subQ0])],"isStart":false})});}
            var sketch = newSketch(context, id + "F21", { "sketchPlane" : qUnion([Q0])});
            skText(sketch, "E209", { "text": "LONDON", "fontName": "OpenSans-Bold.ttf"});
            const initialGuessF21  = {"E209": [0.01422, 0.03775, 1, 0, 0.00276]};
            skSetInitialGuess(sketch, initialGuessF21);
            skSolve(sketch);
        }
        {
            var Q0;
            Q0 = qSketchRegion(id + "F21", true);
            extrude(context, id + "F22", {"entities" : qUnion([Q0]), "operationType" : NewBodyOperationType.ADD, "depth" : 1 * mm, "offsetDistance" : 25 * mm});
        }
        {
            var Q0;
            {var subQ0=sQuery(id+"F4.wireOp",EDGE,"E2.left");var subQ1=sQuery(id+"F4.wireOp",EDGE,"E2.right");Q0=makeQuery(id+"F17.boolean.opBoolean","SPLIT",FACE,{"disambiguationData":[TD([makeQuery(id+"F17.opExtrude","SWEPT_FACE",FACE,{"disambiguationData":[OSD([sQuery(id+"F16.wireOp",EDGE,"E11.top")])]})])],"derivedFrom":makeQuery(id+"F10.opExtrude","CAP_FACE",FACE,{"disambiguationData":[OSD([sQuery(id+"F4.wireOp",EDGE,"E2.bottom"),sQuery(id+"F4.wireOp",EDGE,"E2.top"),subQ0,subQ1])],"isStart":false})});}
            var sketch = newSketch(context, id + "F23", { "sketchPlane" : qUnion([Q0])});
            skLineSegment(sketch, "E210.bottom", {"start": v(20.23, 59.5) * mm, "end": v(26.23, 59.5) * mm});
            skLineSegment(sketch, "E210.top", {"start": v(20.23, 53.5) * mm, "end": v(26.23, 53.5) * mm});
            skLineSegment(sketch, "E210.left", {"start": v(20.23, 59.5) * mm, "end": v(20.23, 53.5) * mm});
            skLineSegment(sketch, "E210.right", {"start": v(26.23, 59.5) * mm, "end": v(26.23, 53.5) * mm});
            skLineSegment(sketch, "E211", {"start": v(-3.5, 56.5) * mm, "end": v(49.97, 56.5) * mm, "construction": true});
            skPoint(sketch, "E212", {"position": v(23.23, 56.5) * mm});
            skLineSegment(sketch, "E213", {"start": v(20.23, 53.5) * mm, "end": v(26.23, 59.5) * mm, "construction": true});
            skSolve(sketch);
        }
        {
            var Q0;
            Q0 = qSketchRegion(id + "F23", true);
            extrude(context, id + "F24", {"entities" : qUnion([Q0]), "operationType" : NewBodyOperationType.ADD, "depth" : 2 * mm, "offsetDistance" : 25 * mm});
        }
        {
            var Q0;
            Q0=makeQuery(id+"F24.opExtrude","SWEPT_EDGE",EDGE,{"disambiguationData":[OSD([sQuery(id+"F23.wireOp",EDGE,"E210.bottom"),sQuery(id+"F23.wireOp",EDGE,"E210.left")])]});
            var Q1;
            Q1=makeQuery(id+"F24.opExtrude","SWEPT_EDGE",EDGE,{"disambiguationData":[OSD([sQuery(id+"F23.wireOp",EDGE,"E210.bottom"),sQuery(id+"F23.wireOp",EDGE,"E210.right")])]});
            var Q2;
            Q2=makeQuery(id+"F24.opExtrude","SWEPT_EDGE",EDGE,{"disambiguationData":[OSD([sQuery(id+"F23.wireOp",EDGE,"E210.top"),sQuery(id+"F23.wireOp",EDGE,"E210.left")])]});
            var Q3;
            Q3=makeQuery(id+"F24.opExtrude","SWEPT_EDGE",EDGE,{"disambiguationData":[OSD([sQuery(id+"F23.wireOp",EDGE,"E210.top"),sQuery(id+"F23.wireOp",EDGE,"E210.right")])]});
            fillet(context, id + "F25", {"entities" : qUnion([Q0, Q1, Q2, Q3]), "radius" : 1.4 * mm, "tangentPropagation" : true, "allowEdgeOverflow" : false});
        }
        {
            var Q0;
            Q0=makeQuery(id+"F24.opExtrude","CAP_FACE",FACE,{"disambiguationData":[OSD([sQuery(id+"F23.wireOp",EDGE,"E210.bottom"),sQuery(id+"F23.wireOp",EDGE,"E210.top"),sQuery(id+"F23.wireOp",EDGE,"E210.left"),sQuery(id+"F23.wireOp",EDGE,"E210.right")])],"isStart":false});
            var sketch = newSketch(context, id + "F26", { "sketchPlane" : qUnion([Q0])});
            skLineSegment(sketch, "E214", {"start": v(20.5, 57.97) * mm, "end": v(20.5, 54.38) * mm, "construction": true});
            skPoint(sketch, "E215", {"position": v(20.5, 56.17) * mm});
            skArc(sketch, "E216", {"start": v(22.88, 54.38) * mm, "mid": v(24.67, 56.17) * mm, "end": v(22.88, 57.97) * mm});
            skLineSegment(sketch, "E217", {"start": v(22.88, 57.97) * mm, "end": v(22.41, 57.97) * mm});
            skLineSegment(sketch, "E218", {"start": v(22.41, 57.97) * mm, "end": v(22.41, 54.38) * mm});
            skLineSegment(sketch, "E219", {"start": v(22.41, 54.38) * mm, "end": v(22.88, 54.38) * mm});
            skSolve(sketch);
        }
        {
            var Q0;
            Q0 = qSketchRegion(id + "F26", true);
            extrude(context, id + "F27", {"entities" : qUnion([Q0]), "operationType" : NewBodyOperationType.REMOVE, "oppositeDirection" : true, "depth" : 2 * mm, "offsetDistance" : 25 * mm});
        }
        {
            var Q0;
            Q0=makeQuery(id+"F11.opExtrude","CAP_EDGE",EDGE,{"disambiguationData":[OSD([sQuery(id+"F8.wireOp",EDGE,"E9")])],"isStart":false});
            var Q1;
            Q1=makeQuery(id+"F9.opExtrude","CAP_EDGE",EDGE,{"disambiguationData":[OSD([sQuery(id+"F6.wireOp",EDGE,"E5")])],"isStart":false});
            var Q2;
            Q2=makeQuery(id+"F12.opExtrude","CAP_EDGE",EDGE,{"disambiguationData":[OSD([sQuery(id+"F1.wireOp",EDGE,"E1.top")])],"isStart":false});
            fillet(context, id + "F28", {"entities" : qUnion([Q0, Q1, Q2]), "radius" : 5 * mm, "tangentPropagation" : true, "allowEdgeOverflow" : false});
        }
    });
